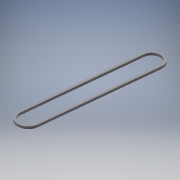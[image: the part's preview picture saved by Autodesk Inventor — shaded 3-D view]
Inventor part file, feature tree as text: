
AUTODESK INVENTOR PART (.ipt)
format: ipt  version: 2017 (Build 210142000, 142)  size: 105,472 bytes
history: native  units: mm
features: other x4, reference x2, extrude x1, sketch x1
ambient origin geometry x8: Origin, YZ Plane, XZ Plane, XY Plane, X Axis, Y Axis, Z Axis, Center Point
bodies: Solid1 (feature_tree)
feature tree (8):
  extrude  "Extrusion1"  Depth=8.0mm TaperAngle=0.0deg
  sketch  "Sketch1"  dims[d0=8.0mm d1=8.0mm d2=0.0mm]
  reference  "Reference1"
  reference  "Reference2"
  other  "<userpath>\OneDrive\Inventor\VolledigGeassembleerdv001.iam"
  other  "VolledigGeassembleerdv001.iam"
  other  "aandrijfMotor:1"
  other  "kettingwiel:3"
